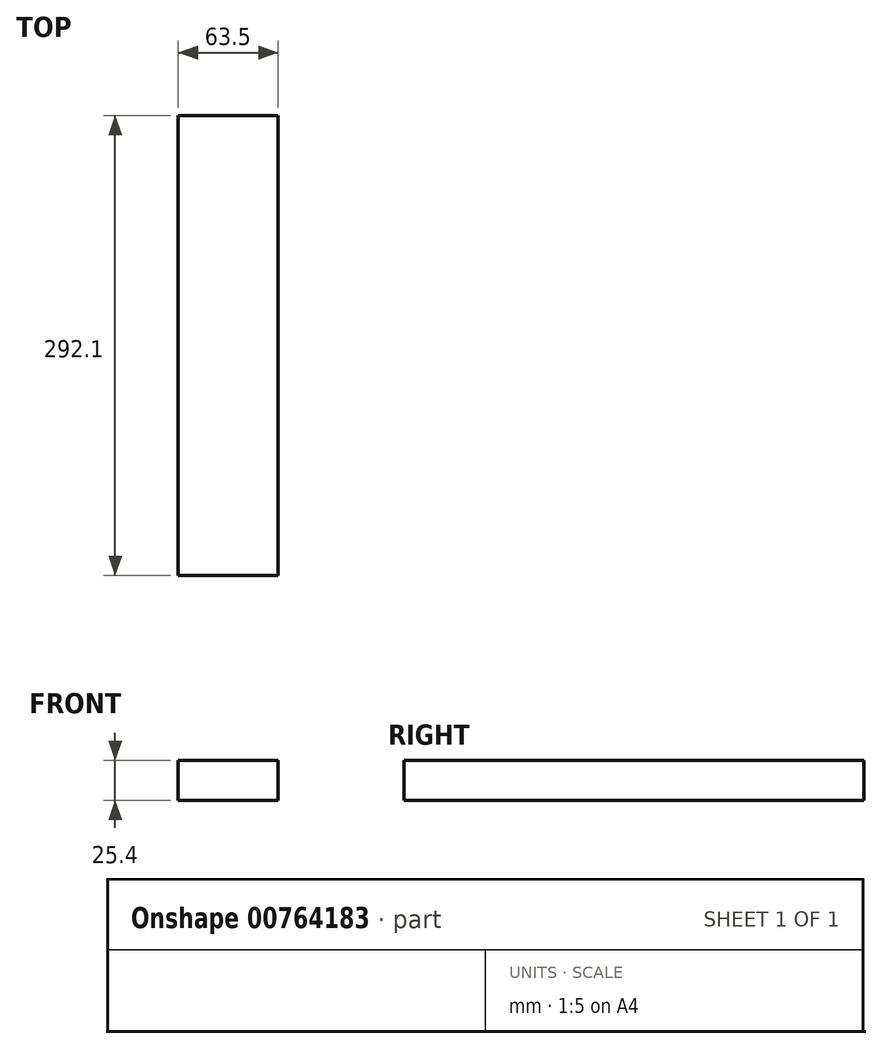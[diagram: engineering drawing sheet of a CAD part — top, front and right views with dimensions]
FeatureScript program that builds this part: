
annotation { "Feature Type Name" : "Feature", "Feature Type Description" : "" }
export const myFeature = defineFeature(function(context is Context, id is Id, definition is map)
    precondition{}
    {
        {
            var Q0;
            Q0=qCreatedBy(makeId("Front.planeOp"),FACE);
            var sketch = newSketch(context, id + "F0", { "sketchPlane" : qUnion([Q0])});
            skLineSegment(sketch, "E0.bottom", {"start": v(0, 0) * mm, "end": v(63.5, 0) * mm});
            skLineSegment(sketch, "E0.top", {"start": v(0, 25.4) * mm, "end": v(63.5, 25.4) * mm});
            skLineSegment(sketch, "E0.left", {"start": v(0, 0) * mm, "end": v(0, 25.4) * mm});
            skLineSegment(sketch, "E0.right", {"start": v(63.5, 0) * mm, "end": v(63.5, 25.4) * mm});
            skSolve(sketch);
        }
        {
            var Q0;
            Q0=makeQuery(id+"F0.imprint","IMPRINT",FACE,{"disambiguationData":[TD([[makeQuery(id+"F0.imprint","IMPRINT",EDGE,{"derivedFrom":sQuery(id+"F0.wireOp",EDGE,"E0.bottom")}),1.0]])]});
            extrude(context, id + "F1", {"entities" : qUnion([Q0]), "depth" : 292.1 * mm, "offsetDistance" : 25.4 * mm});
        }
    });
